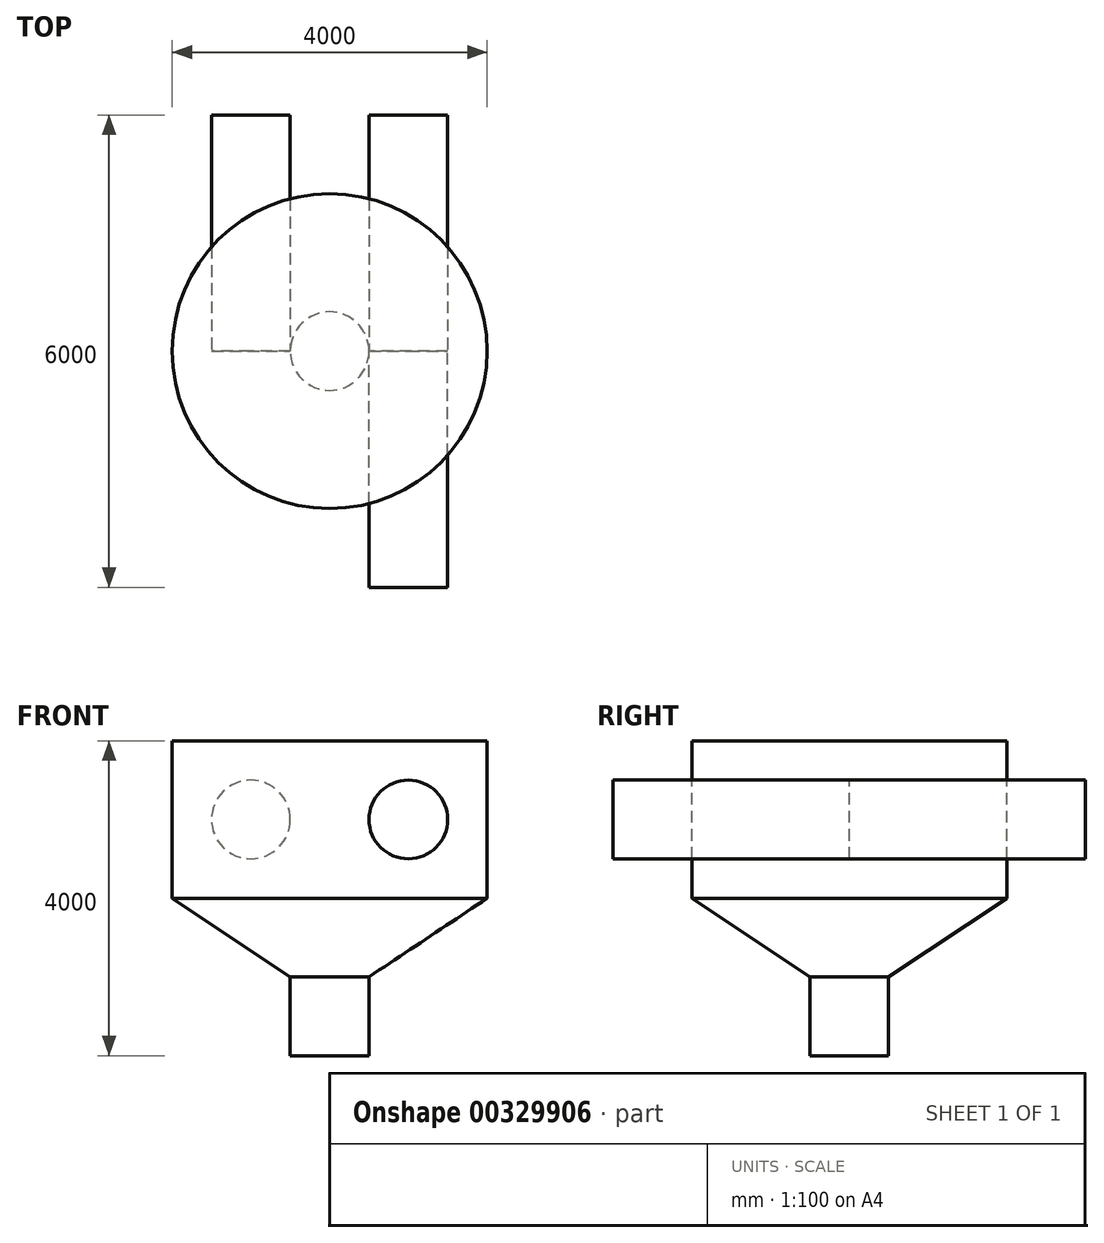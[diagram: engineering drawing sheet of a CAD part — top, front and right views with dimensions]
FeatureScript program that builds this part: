
annotation { "Feature Type Name" : "Feature", "Feature Type Description" : "" }
export const myFeature = defineFeature(function(context is Context, id is Id, definition is map)
    precondition{}
    {
        {
            var Q0;
            Q0=qCreatedBy(makeId("Front.planeOp"),FACE);
            var sketch = newSketch(context, id + "F0", { "sketchPlane" : qUnion([Q0])});
            skLineSegment(sketch, "E0", {"start": v(0, 2000) * mm, "end": v(2000, 2000) * mm});
            skLineSegment(sketch, "E1", {"start": v(2000, 2000) * mm, "end": v(2000, 0) * mm});
            skLineSegment(sketch, "E2", {"start": v(2000, 0) * mm, "end": v(500, -1000) * mm});
            skLineSegment(sketch, "E3", {"start": v(500, -1000) * mm, "end": v(500, -2000) * mm});
            skLineSegment(sketch, "E4", {"start": v(500, -2000) * mm, "end": v(0, -2000) * mm});
            skLineSegment(sketch, "E5", {"start": v(0, 2000) * mm, "end": v(0, -2000) * mm});
            skSolve(sketch);
        }
        {
            var Q0;
            Q0 = qSketchRegion(id + "F0", true);
            var Q1;
            Q1=sQuery(id+"F0.wireOp",EDGE,"E5");
            revolve(context, id + "F1", {"entities" : qUnion([Q0]), "axis" : qUnion([Q1]), "revolveType" : RevolveType.FULL});
        }
        {
            var Q0;
            Q0=qCreatedBy(makeId("Front.planeOp"),FACE);
            var sketch = newSketch(context, id + "F2", { "sketchPlane" : qUnion([Q0])});
            skCircle(sketch, "E6", {"center": v(1000, 1000) * mm, "radius": 500 * mm});
            skSolve(sketch);
        }
        {
            var Q0;
            Q0 = qSketchRegion(id + "F2", true);
            extrude(context, id + "F3", {"entities" : qUnion([Q0]), "depth" : 3000 * mm});
        }
        {
            var Q0;
            Q0=makeQuery(id+"F3.opExtrude","SWEPT_BODY",BODY,{"disambiguationData":[OSD([sQuery(id+"F2.wireOp",EDGE,"E6")])]});
            var Q1;
            Q1=qCreatedBy(makeId("Front.planeOp"),FACE);
            mirror(context, id + "F4", {"entities" : qUnion([Q0]), "mirrorPlane" : qUnion([Q1])});
        }
        {
            var Q0;
            Q0=makeQuery(id+"F4.opPattern","COPY",BODY,{"derivedFrom":makeQuery(id+"F3.opExtrude","SWEPT_BODY",BODY,{"disambiguationData":[OSD([sQuery(id+"F2.wireOp",EDGE,"E6")])]}),"instanceName":"1"});
            var Q1;
            Q1=qCreatedBy(makeId("Right.planeOp"),FACE);
            mirror(context, id + "F5", {"entities" : qUnion([Q0]), "mirrorPlane" : qUnion([Q1])});
        }
    });
